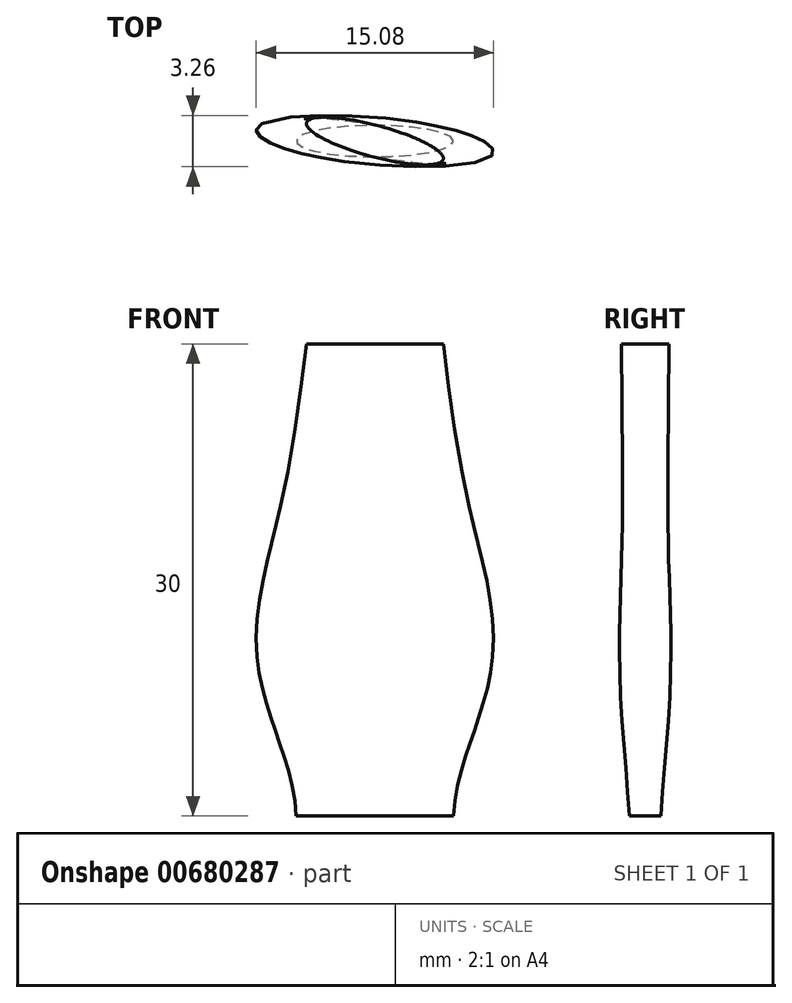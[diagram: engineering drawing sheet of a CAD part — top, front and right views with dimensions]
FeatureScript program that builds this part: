
annotation { "Feature Type Name" : "Feature", "Feature Type Description" : "" }
export const myFeature = defineFeature(function(context is Context, id is Id, definition is map)
    precondition{}
    {
        {
            var Q0;
            Q0=qCreatedBy(makeId("Top.planeOp"),FACE);
            cPlane(context, id + "F0", {"entities" : qUnion([Q0]), "cplaneType" : CPlaneType.OFFSET, "offset" : 10 * mm, "width" : 150 * mm, "height" : 150 * mm});
        }
        {
            var Q0;
            Q0=qCreatedBy(id+"F0.planeOp",FACE);
            cPlane(context, id + "F1", {"entities" : qUnion([Q0]), "cplaneType" : CPlaneType.OFFSET, "offset" : 10 * mm, "width" : 150 * mm, "height" : 150 * mm});
        }
        {
            var Q0;
            Q0=qCreatedBy(id+"F1.planeOp",FACE);
            cPlane(context, id + "F2", {"entities" : qUnion([Q0]), "cplaneType" : CPlaneType.OFFSET, "offset" : 10 * mm, "width" : 150 * mm, "height" : 150 * mm});
        }
        {
            var Q0;
            Q0=qCreatedBy(makeId("Top.planeOp"),FACE);
            var sketch = newSketch(context, id + "F3", { "sketchPlane" : qUnion([Q0])});
            skEllipse(sketch, "E0", {"center": v(0, 0) * mm, "majorRadius": 5 * mm, "minorRadius": 1 * mm, "majorAxis": v(1, 0)});
            skSolve(sketch);
        }
        {
            var Q0;
            Q0=qCreatedBy(id+"F0.planeOp",FACE);
            var sketch = newSketch(context, id + "F4", { "sketchPlane" : qUnion([Q0])});
            skEllipse(sketch, "E1", {"center": v(0, 0) * mm, "majorRadius": 7.5 * mm, "minorRadius": 1.5 * mm, "majorAxis": v(1, -0.09)});
            skSolve(sketch);
        }
        {
            var Q0;
            Q0=qCreatedBy(id+"F1.planeOp",FACE);
            var sketch = newSketch(context, id + "F5", { "sketchPlane" : qUnion([Q0])});
            skEllipse(sketch, "E2", {"center": v(0, 0) * mm, "majorRadius": 6 * mm, "minorRadius": 1 * mm, "majorAxis": v(0.98, -0.17)});
            skSolve(sketch);
        }
        {
            var Q0;
            Q0=qCreatedBy(id+"F2.planeOp",FACE);
            var sketch = newSketch(context, id + "F6", { "sketchPlane" : qUnion([Q0])});
            skEllipse(sketch, "E3", {"center": v(0, 0) * mm, "majorRadius": 4.5 * mm, "minorRadius": 1 * mm, "majorAxis": v(0.97, -0.26)});
            skSolve(sketch);
        }
        {
            var Q0;
            Q0=makeQuery(id+"F3.imprint","IMPRINT",FACE,{"disambiguationData":[TD([[makeQuery(id+"F3.imprint","IMPRINT",EDGE,{"derivedFrom":sQuery(id+"F3.wireOp",EDGE,"E0")}),1.0]])]});
            var Q1;
            Q1=makeQuery(id+"F4.imprint","IMPRINT",FACE,{"disambiguationData":[TD([[makeQuery(id+"F4.imprint","IMPRINT",EDGE,{"derivedFrom":sQuery(id+"F4.wireOp",EDGE,"E1")}),1.0]])]});
            var Q2;
            Q2=makeQuery(id+"F5.imprint","IMPRINT",FACE,{"disambiguationData":[TD([[makeQuery(id+"F5.imprint","IMPRINT",EDGE,{"derivedFrom":sQuery(id+"F5.wireOp",EDGE,"E2")}),1.0]])]});
            var Q3;
            Q3=makeQuery(id+"F6.imprint","IMPRINT",FACE,{"disambiguationData":[TD([[makeQuery(id+"F6.imprint","IMPRINT",EDGE,{"derivedFrom":sQuery(id+"F6.wireOp",EDGE,"E3")}),1.0]])]});
            loft(context, id + "F7", {"sheetProfilesArray" : [{ "sheetProfileEntities" : qUnion([Q0]) }, { "sheetProfileEntities" : qUnion([Q1]) }, { "sheetProfileEntities" : qUnion([Q2]) }, { "sheetProfileEntities" : qUnion([Q3]) }]});
        }
    });
